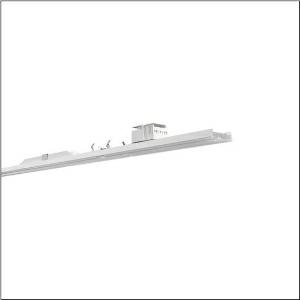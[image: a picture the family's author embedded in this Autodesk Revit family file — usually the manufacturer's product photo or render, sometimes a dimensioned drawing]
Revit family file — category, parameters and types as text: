
# Revit family: licross_r__11_recessed_mo_51tl14cn475f_596f
name_source: partatom
category: Lighting Fixtures
units: mm (PartAtom-declared; Revit-internal decimal feet)

## family parameters
Cut with Voids When Loaded = No
Host = Face
Light Source = No
Part Type = Normal
Room Calculation Point = No
Round Connector Dimension = Use Diameter
Shared = No

## types (1)
- --- (1 x LED, 7640 lm, 48 W, 4000K)
    Apparent Load = 48 VA
    CIE Flux Codes = 56 84 97 100 100
    Color Rendering = 80
    Color Temperature = 4000K
    Default Elevation = 1800 mm
    Description = Licross® 11 Recessed MOluminaire insert, length: 1.500mm, width: 66mm, height: 67mm, LED rated luminous flux: 7.640lm, light colour: 840, control gear: ON/OFF Multilumen, CLOi, control gear: ECG Multilumen, with plug, 3-pole, with phase selection, mains connection: 220..240V, AC, 50/60Hz, halogen-free wiring, primary optical cover: cover, of PMMA, light emission: direct distribution, primary light characteristic: asymmetric, protection rating (complete): IP40, insulation class (complete): insulation class I (protective earthing), certification: CE, ENEC, VDE, protection symbol: D if used in an environment without relevant dust loads with corresponding accessories, permissible ambient temperature for indoor applications: -35..+40°C, reducing of maximum allowable ambient temperature of 5°C with ceiling mounting, corresponds to IFS (International Featured Standards) requirements for safety and quality in the food industry, packaging unit: 1 piece
    Height = 58 mm
    Lamp = 1 x LED
    Lamp Light Flux = 7640 lm
    Lamp Power = 48 W
    Lamp count = 1
    Length = 1500 mm
    Luminous efficacy = 159 lm/W
    Manufacturer = Siteco
    ModVariant = No
    Model = 51TL14CN475F
    Mounting Place = Ceiling
    Mounting Type = Pendant
    Number of Poles = 1
    OnlyDefault = Yes
    Power Factor = 1
    Product Name = Licross® 11 Recessed MO
    Product group = luminaire insert
    ProductGroupID = 902
    Protection Class = Protection class I
    Protection Degree = IP 40
    RLX_Detail_Level = 1
    RlxData = <blob elided: 20589 chars, md5=a6d4f22b>
    Socket = socket
    Standby Power = 0 W
    System Light Flux = 7640 lm
    System Power = 48 W
    Type Comments = factory setting: luminous flux: 100 % | (A | C | E) | 109 mA
    Type Image = l_1266722.jpg
    URL = http://relux.com
    VarID = @adj_138903
    Voltage = 0 V
    Weight = 0.00 kg
    Width = 66 mm

## geometry (parser evidence)
native form markers: Blend x4, Sweep x11
no freeform markers — native parametric forms only
